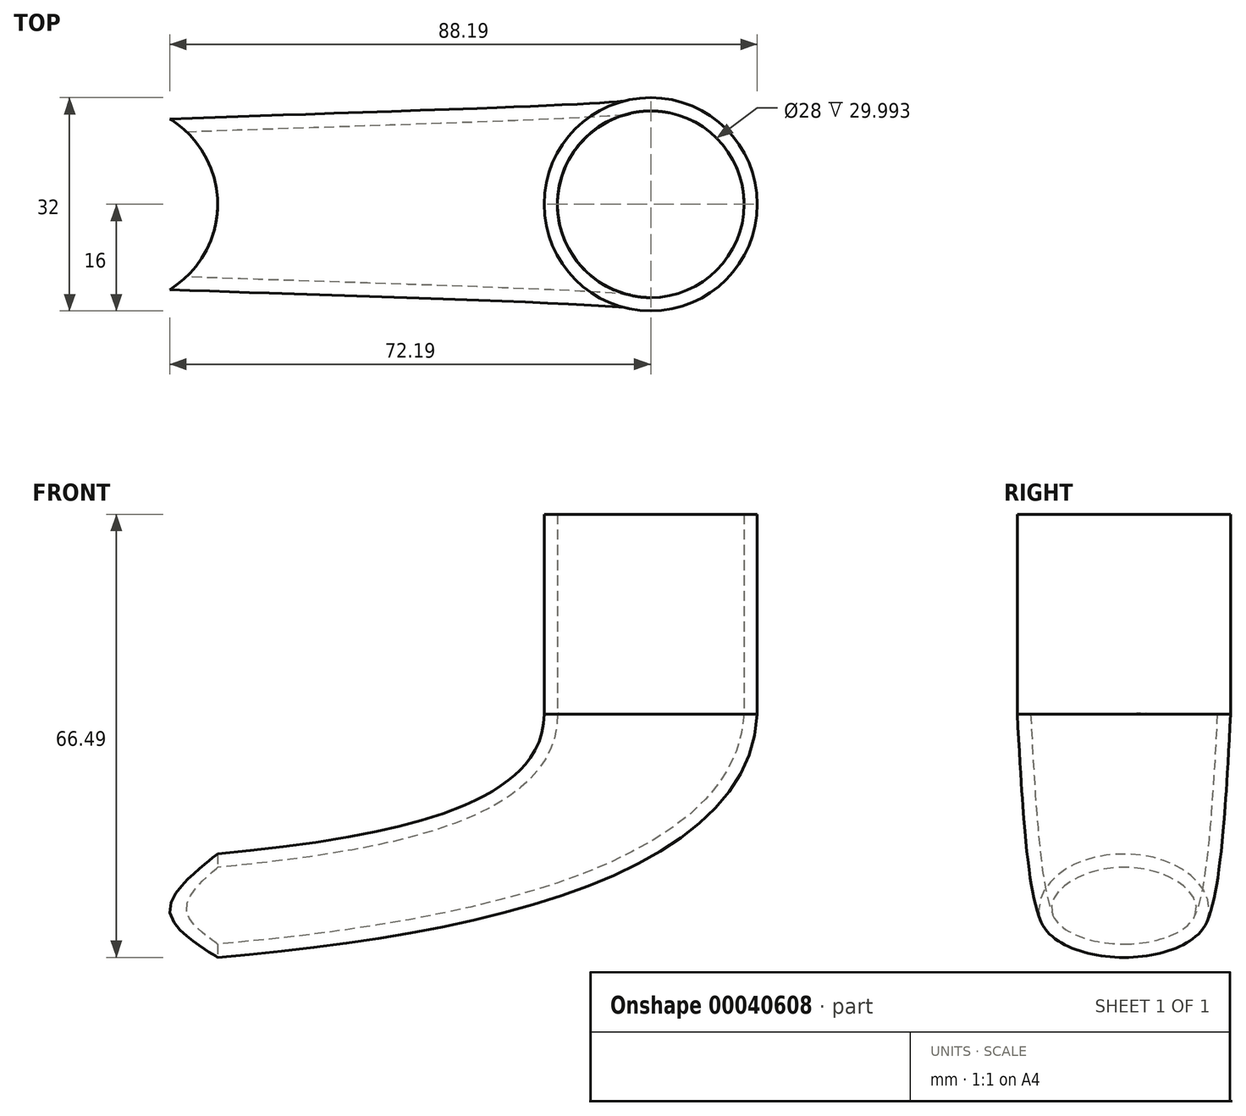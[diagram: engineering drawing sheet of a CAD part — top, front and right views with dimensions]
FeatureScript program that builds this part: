
annotation { "Feature Type Name" : "Feature", "Feature Type Description" : "" }
export const myFeature = defineFeature(function(context is Context, id is Id, definition is map)
    precondition{}
    {
        {
            var Q0;
            Q0=qCreatedBy(makeId("Top.planeOp"),FACE);
            var sketch = newSketch(context, id + "F0", { "sketchPlane" : qUnion([Q0])});
            skLineSegment(sketch, "E0", {"start": v(-83.02, 0) * mm, "end": v(78.58, 0) * mm, "construction": true});
            skArc(sketch, "E1", {"start": v(-16, 0) * mm, "mid": v(0, -16) * mm, "end": v(16, 0) * mm});
            skArc(sketch, "E2", {"start": v(16, 0) * mm, "mid": v(0, 16) * mm, "end": v(-16, 0) * mm});
            skLineSegment(sketch, "E3", {"start": v(0, 24.3) * mm, "end": v(0, 16) * mm, "construction": true});
            skPoint(sketch, "E3.endSnap0", {"position": v(0, -16) * mm});
            skLineSegment(sketch, "E4", {"start": v(0, 16) * mm, "end": v(0, -16) * mm, "construction": true});
            skLineSegment(sketch, "E5", {"start": v(0, -16) * mm, "end": v(0, -22.18) * mm, "construction": true});
            skSolve(sketch);
        }
        {
            var Q0;
            Q0=qCreatedBy(makeId("Right.planeOp"),FACE);
            cPlane(context, id + "F1", {"entities" : qUnion([Q0]), "cplaneType" : CPlaneType.OFFSET, "offset" : 80 * mm, "oppositeDirection" : true, "width" : 150 * mm, "height" : 150 * mm});
        }
        {
            var Q0;
            Q0=qCreatedBy(id+"F1.planeOp",FACE);
            var sketch = newSketch(context, id + "F2", { "sketchPlane" : qUnion([Q0])});
            skEllipticalArc(sketch, "E6", {});
            skEllipticalArc(sketch, "E7", {});
            skEllipticalArc(sketch, "E8", {});
            skEllipticalArc(sketch, "E9", {});
            skLineSegment(sketch, "E10.0", {"start": v(16, 0) * mm, "end": v(-16, 0) * mm, "construction": true});
            const initialGuessF2  = {"E6": [0, -0.03, 1, 0, 0.0125, 0.0075, 3.141592653589793, 4.71238898038469], "E7": [0, -0.03, 1, 0, 0.0125, 0.0075, 0, 1.5707963267948966], "E8": [0, -0.03, 1, 0, 0.0125, 0.0075, 1.5707963267948966, 3.141592653589793], "E9": [0, -0.03, 1, 0, 0.0125, 0.0075, 4.71238898038469, 0]};
            skSetInitialGuess(sketch, initialGuessF2);
            skSolve(sketch);
        }
        {
            var Q0;
            Q0=qCreatedBy(makeId("Front.planeOp"),FACE);
            var sketch = newSketch(context, id + "F3", { "sketchPlane" : qUnion([Q0])});
            skFitSpline(sketch, "E11", {"points": [v(-80, -22.5) * mm, v(-16, 0) * mm], "startDerivative": vector(54.69, 7.04) * mm, "endDerivative": vector(-0.44, 57.87) * mm});
            skFitSpline(sketch, "E12", {"points": [v(-80, -37.5) * mm, v(16, 0) * mm], "startDerivative": vector(113.7, 5.9) * mm, "endDerivative": vector(4.22, 85.94) * mm});
            skSolve(sketch);
        }
        {
            var Q0;
            Q0=makeQuery(id+"F0.imprint","IMPRINT",FACE,{"disambiguationData":[TD([[makeQuery(id+"F0.imprint","IMPRINT",EDGE,{"derivedFrom":sQuery(id+"F0.wireOp",EDGE,"E1")}),1.0]])]});
            var Q1;
            Q1=makeQuery(id+"F2.imprint","IMPRINT",FACE,{"disambiguationData":[TD([[makeQuery(id+"F2.imprint","IMPRINT",EDGE,{"derivedFrom":sQuery(id+"F2.wireOp",EDGE,"E6")}),1.0]])]});
            var Q2;
            Q2=sQuery(id+"F3.wireOp",EDGE,"E12");
            var Q3;
            Q3=sQuery(id+"F3.wireOp",EDGE,"E11");
            loft(context, id + "F4", {"addGuides" : true, "sheetProfilesArray" : [{ "sheetProfileEntities" : qUnion([Q0]) }, { "sheetProfileEntities" : qUnion([Q1]) }], "guidesArray" : [{ "guideEntities" : qUnion([Q2]), "guideDerivativeType" : LoftGuideDerivativeType.DEFAULT, "guideDerivativeMagnitude" : 1 }, { "guideEntities" : qUnion([Q3]), "guideDerivativeType" : LoftGuideDerivativeType.DEFAULT, "guideDerivativeMagnitude" : 1 }]});
        }
        {
            var Q0;
            Q0=makeQuery(id+"F0.imprint","IMPRINT",FACE,{"disambiguationData":[TD([[makeQuery(id+"F0.imprint","IMPRINT",EDGE,{"derivedFrom":sQuery(id+"F0.wireOp",EDGE,"E1")}),1.0]])]});
            extrude(context, id + "F5", {"entities" : qUnion([Q0]), "operationType" : NewBodyOperationType.ADD, "depth" : 30 * mm});
        }
        {
            var Q0;
            Q0=qCreatedBy(makeId("Top.planeOp"),FACE);
            var Q1;
            Q1=sQuery(id+"F2.wireOp",VERTEX,"E6.center");
            cPlane(context, id + "F6", {"entities" : qUnion([Q0, Q1]), "cplaneType" : CPlaneType.PLANE_POINT, "offset" : 25 * mm, "width" : 150 * mm, "height" : 150 * mm});
        }
        {
            var Q0;
            Q0=qCreatedBy(id+"F6.planeOp",FACE);
            var sketch = newSketch(context, id + "F7", { "sketchPlane" : qUnion([Q0])});
            skPoint(sketch, "E13.0", {"position": v(-80, 0) * mm});
            skCircle(sketch, "E14", {"center": v(-80, 0) * mm, "radius": 15 * mm});
            skPoint(sketch, "E15.0", {"position": v(-80, -12.5) * mm});
            skSolve(sketch);
        }
        {
            var Q0;
            Q0=makeQuery(id+"F7.imprint","IMPRINT",FACE,{"disambiguationData":[TD([[makeQuery(id+"F7.imprint","IMPRINT",EDGE,{"derivedFrom":sQuery(id+"F7.wireOp",EDGE,"E14")}),1.0]])]});
            extrude(context, id + "F8", {"entities" : qUnion([Q0]), "depth" : 40 * mm, "symmetric" : true});
        }
        {
            var Q0;
            Q0=makeQuery(id+"F5.opExtrude","CAP_FACE",FACE,{"disambiguationData":[OSD([sQuery(id+"F0.wireOp",EDGE,"E1"),sQuery(id+"F0.wireOp",EDGE,"E2")])],"isStart":false});
            var Q1;
            Q1=makeQuery(id+"F4.opLoft","SWEPT_BODY",BODY,{"disambiguationData":[OSD([makeQuery(id+"F0.imprint","IMPRINT",FACE,{"disambiguationData":[TD([[makeQuery(id+"F0.imprint","IMPRINT",EDGE,{"derivedFrom":sQuery(id+"F0.wireOp",EDGE,"E1")}),1.0]])]}),makeQuery(id+"F2.imprint","IMPRINT",FACE,{"disambiguationData":[TD([[makeQuery(id+"F2.imprint","IMPRINT",EDGE,{"derivedFrom":sQuery(id+"F2.wireOp",EDGE,"E6")}),1.0]])]}),sQuery(id+"F3.wireOp",EDGE,"E11"),sQuery(id+"F3.wireOp",EDGE,"E12")])]});
            shell(context, id + "F9", {"entities" : qUnion([Q0]), "parts" : qUnion([Q1]), "thickness" : 2 * mm});
        }
        {
            var Q0;
            Q0=makeQuery(id+"F8.opExtrude","SWEPT_BODY",BODY,{"disambiguationData":[OSD([sQuery(id+"F7.wireOp",EDGE,"E14")])]});
            var Q1;
            Q1=makeQuery(id+"F4.opLoft","SWEPT_BODY",BODY,{"disambiguationData":[OSD([makeQuery(id+"F0.imprint","IMPRINT",FACE,{"disambiguationData":[TD([[makeQuery(id+"F0.imprint","IMPRINT",EDGE,{"derivedFrom":sQuery(id+"F0.wireOp",EDGE,"E1")}),1.0]])]}),makeQuery(id+"F2.imprint","IMPRINT",FACE,{"disambiguationData":[TD([[makeQuery(id+"F2.imprint","IMPRINT",EDGE,{"derivedFrom":sQuery(id+"F2.wireOp",EDGE,"E6")}),1.0]])]}),sQuery(id+"F3.wireOp",EDGE,"E11"),sQuery(id+"F3.wireOp",EDGE,"E12")])]});
            booleanBodies(context, id + "F10", {"operationType" : BooleanOperationType.SUBTRACTION, "tools" : qUnion([Q0]), "targets" : qUnion([Q1])});
        }
    });
